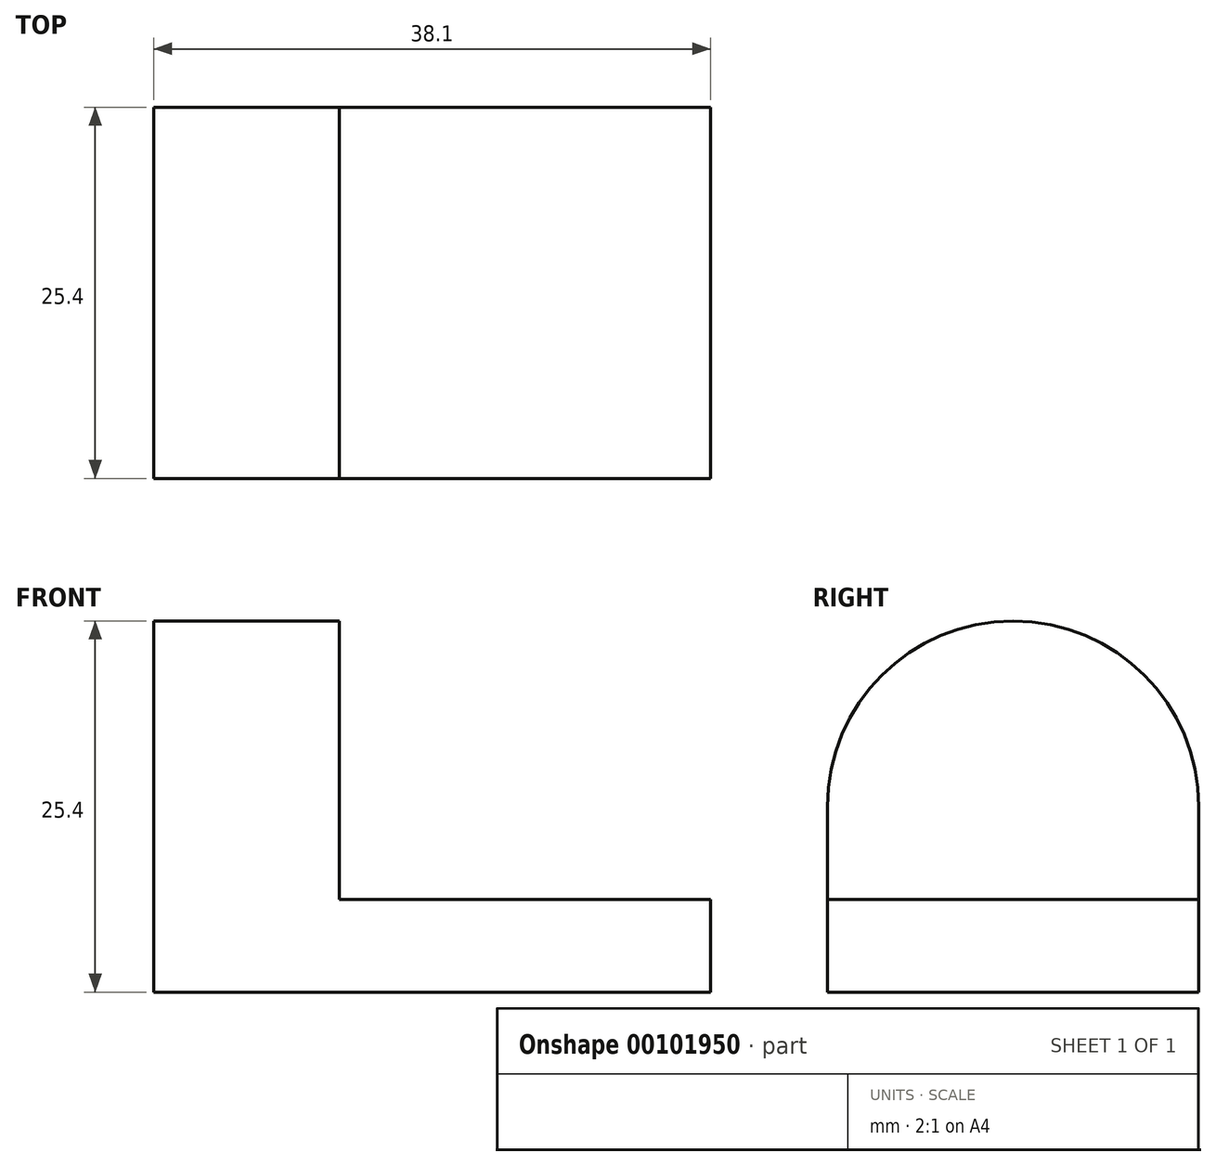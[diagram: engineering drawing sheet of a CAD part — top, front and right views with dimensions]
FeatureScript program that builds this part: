
annotation { "Feature Type Name" : "Feature", "Feature Type Description" : "" }
export const myFeature = defineFeature(function(context is Context, id is Id, definition is map)
    precondition{}
    {
        {
            var Q0;
            Q0=qCreatedBy(makeId("Front.planeOp"),FACE);
            var sketch = newSketch(context, id + "F0", { "sketchPlane" : qUnion([Q0])});
            skLineSegment(sketch, "E0", {"start": v(0, 0) * mm, "end": v(38.1, 0) * mm});
            skLineSegment(sketch, "E1", {"start": v(38.1, 0) * mm, "end": v(38.1, 6.35) * mm});
            skLineSegment(sketch, "E2", {"start": v(38.1, 6.35) * mm, "end": v(12.7, 6.35) * mm});
            skLineSegment(sketch, "E3", {"start": v(12.7, 6.35) * mm, "end": v(12.7, 12.7) * mm});
            skLineSegment(sketch, "E4", {"start": v(12.7, 12.7) * mm, "end": v(0, 12.7) * mm});
            skLineSegment(sketch, "E5", {"start": v(0, 12.7) * mm, "end": v(0, 0) * mm});
            skSolve(sketch);
        }
        {
            var Q0;
            Q0=makeQuery(id+"F0.imprint","IMPRINT",FACE,{"disambiguationData":[TD([[makeQuery(id+"F0.imprint","IMPRINT",EDGE,{"derivedFrom":sQuery(id+"F0.wireOp",EDGE,"E0")}),1.0]])]});
            extrude(context, id + "F1", {"entities" : qUnion([Q0]), "oppositeDirection" : true, "depth" : 25.4 * mm});
        }
        {
            var Q0;
            Q0=makeQuery(id+"F1.opExtrude","SWEPT_FACE",FACE,{"disambiguationData":[OSD([sQuery(id+"F0.wireOp",EDGE,"E5")])]});
            var sketch = newSketch(context, id + "F2", { "sketchPlane" : qUnion([Q0])});
            skArc(sketch, "E6", {"start": v(0, 12.7) * mm, "mid": v(-12.7, 25.4) * mm, "end": v(-25.4, 12.7) * mm});
            skSolve(sketch);
        }
        {
            var Q0;
            Q0=makeQuery(id+"F2.imprint","IMPRINT",FACE,{"disambiguationData":[TD([[makeQuery(id+"F2.imprint","IMPRINT",EDGE,{"derivedFrom":sQuery(id+"F2.wireOp",EDGE,"E6")}),1.0]])]});
            extrude(context, id + "F3", {"entities" : qUnion([Q0]), "operationType" : NewBodyOperationType.ADD, "oppositeDirection" : true, "depth" : 12.7 * mm});
        }
    });
